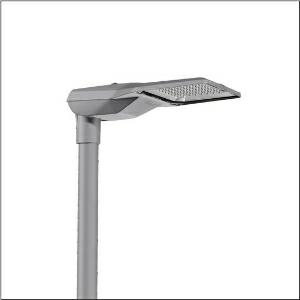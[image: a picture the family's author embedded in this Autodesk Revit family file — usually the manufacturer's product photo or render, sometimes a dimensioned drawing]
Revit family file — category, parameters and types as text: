
# Revit family: streetlight_sl_21_iq_midi___p0_5a_5xe3v31v08nb_978c
name_source: partatom
category: Lighting Fixtures
units: mm (PartAtom-declared; Revit-internal decimal feet)

## family parameters
Cut with Voids When Loaded = No
Host = Face
Light Source = No
Part Type = Normal
Room Calculation Point = No
Round Connector Dimension = Use Diameter
Shared = No

## types (1)
- --- (1 x LED, 21180 lm, 136.6 W, 3000K)
    Apparent Load = 137 VA
    CIE Flux Codes = 37 73 96 100 100
    Color Rendering = 70
    Color Temperature = 3000K
    Default Elevation = 1800 mm
    Description = Streetlight SL 21 iQ midi, mast luminaire, primary light control with lens, of PMMA, primary optical cover: cover, of toughened safety glass, transparent, light distribution: P0.5a, light emission: direct distribution, primary light characteristic: asymmetric, installation type: post-top, side-entry, LED, High Power LED, rated luminous flux: 21.180lm, luminous efficacy: 155lm/W, light colour: 730, colour temperature: 3000K, control gear: iQ-Street Remote, D4i with power reduction, control: pre-setting: logarithmic dimming characteristic, Street-Remote, Auto-Match, Temp-Guard, Lumen-Switch, Night-Set, Smart-Wire, Light-Fading, Desk-Remote (wireless, voltage-free reading and setting of iQ features in the workshop via application-optimized NFC function/RFID function), optimised constant luminous flux control (CLO 2.0), mains connection: 230..240V, AC, 50/60Hz, start of lifetime: 137W, end of service life: 144W, reduction: 61W, luminaire housing, of diecast aluminium, powder-coated, Siteco® metallic grey (DB 702S), corrosivity category C5 mid according to DIN EN ISO 12944, please order mast flange separately, inclination adjustable: 0°, 5°, 10°, 15°, sealing non-destructively replaceable, multi-level sealing system, length: 644mm, width: 335mm, height: 110mm, mast flange for spigot size: 42mm (side-entry): 5XC10008XM4, 60/48mm (side-entry/post-top): 5XC10108XM2, 76/60mm (side-entry/post-top): 5XC10108XM1, mounting height: 4..8m, Smart Interface above, protection rating (complete): IP66, insulation class (complete): insulation class II (safety insulation), certification: CE, ENEC, ENEC+, VDE, impact resistance: IK10, permissible operating ambient temperature for outdoor applications: -40..+50°C, standard-compliant lighting for roads and squares, packaging unit: 1 piece

Light Distribution: P0.5a
    Height = 111 mm
    Lamp = 1 x LED
    Lamp Light Flux = 21180 lm
    Lamp Power = 136.6 W
    Lamp count = 1
    Length = 644 mm
    Luminous efficacy = 155 lm/W
    Manufacturer = Siteco
    ModVariant = No
    Model = 5XE3V31V08NB
    Number of Poles = 1
    OnlyDefault = Yes
    Power Factor = 1
    Product Name = Streetlight SL 21 iQ midi | P0.5a
    Product group = mast luminaire | pylon top
    ProductGroupID = 6100
    Protection Class = Protection class II
    Protection Degree = IP 66
    RLX_Detail_Level = 1
    RLX_Emergency_Light_Flux = 0 lm
    RLX_Emergency_Type = 0
    RLX_Emergency_Type_DB = No
    RlxData = <blob elided: 90513 chars, md5=da117979>
    Socket = socket
    Standby Power = 0 W
    System Light Flux = 21180 lm
    System Power = 137 W
    Type Comments = factory setting: luminous flux: 100 % | dim-lin: 254 | 733 mA
    Type Image = l_1004302.jpg
    URL = http://relux.com
    VarID = @adj_090835
    Voltage = 0 V
    Weight = 0.00 kg
    Width = 336 mm

## geometry (parser evidence)
native form markers: Blend x4, Sweep x11
no freeform markers — native parametric forms only
